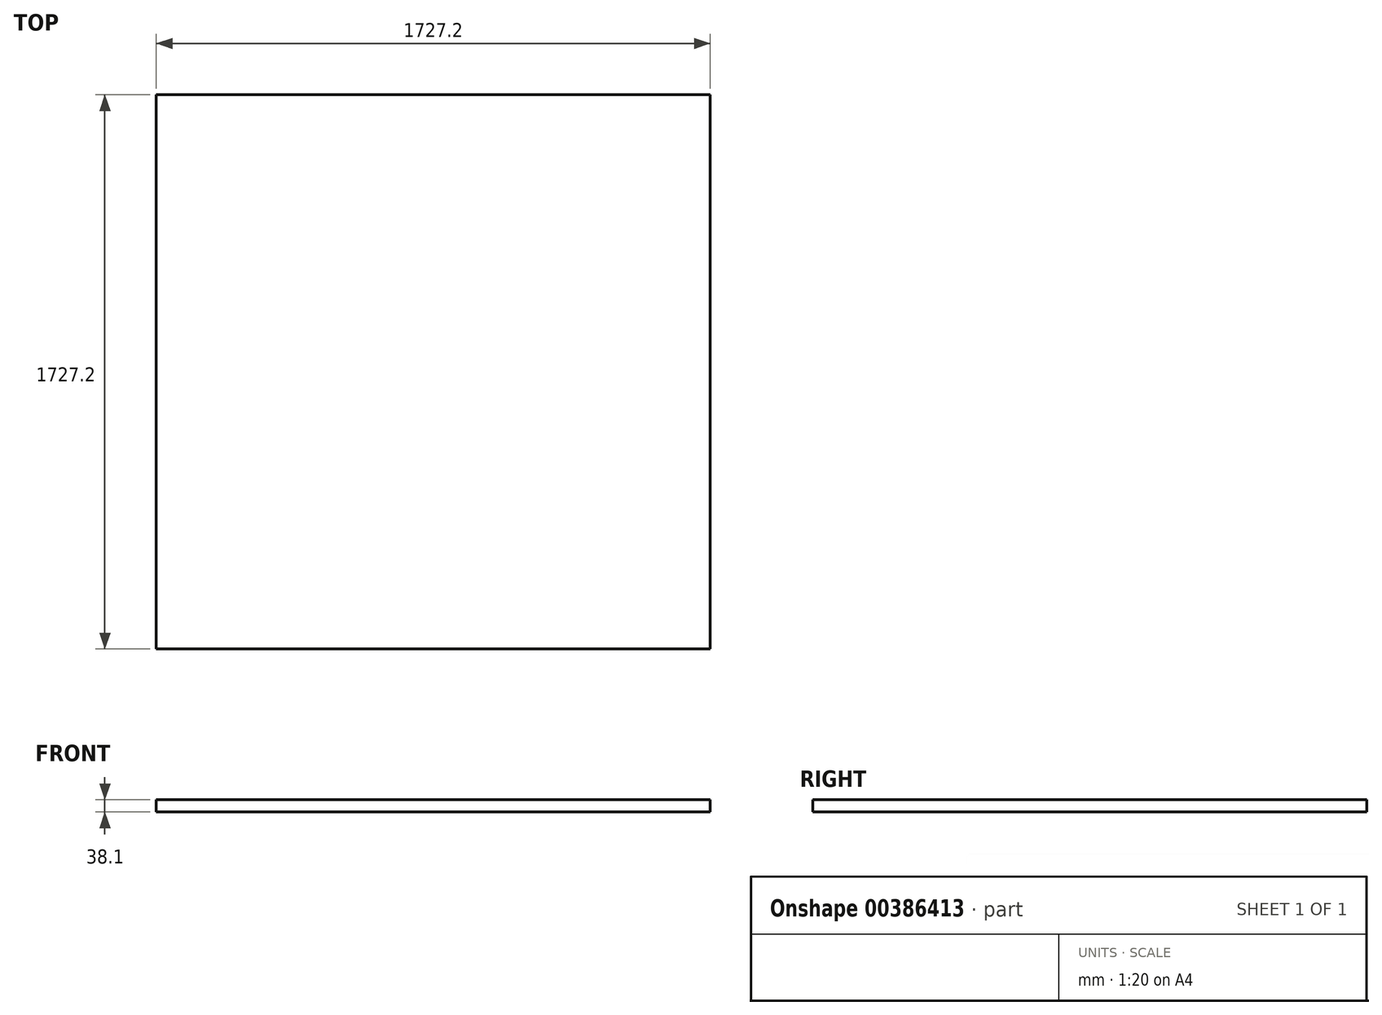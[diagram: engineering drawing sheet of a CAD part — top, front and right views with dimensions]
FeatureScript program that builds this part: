
annotation { "Feature Type Name" : "Feature", "Feature Type Description" : "" }
export const myFeature = defineFeature(function(context is Context, id is Id, definition is map)
    precondition{}
    {
        {
            var Q0;
            Q0=qCreatedBy(makeId("Top.planeOp"),FACE);
            var sketch = newSketch(context, id + "F0", { "sketchPlane" : qUnion([Q0])});
            skLineSegment(sketch, "E0.bottom", {"start": v(-863.6, 863.6) * mm, "end": v(863.6, 863.6) * mm});
            skLineSegment(sketch, "E0.top", {"start": v(-863.6, -863.6) * mm, "end": v(863.6, -863.6) * mm});
            skLineSegment(sketch, "E0.left", {"start": v(-863.6, 863.6) * mm, "end": v(-863.6, -863.6) * mm});
            skLineSegment(sketch, "E0.right", {"start": v(863.6, 863.6) * mm, "end": v(863.6, -863.6) * mm});
            skPoint(sketch, "E0.middle", {"position": v(0, 0) * mm});
            skSolve(sketch);
        }
        {
            var Q0;
            Q0 = qSketchRegion(id + "F0", true);
            extrude(context, id + "F1", {"entities" : qUnion([Q0]), "depth" : 38.1 * mm});
        }
        {
            var Q0;
            Q0=makeQuery(id+"F1.opExtrude","CAP_FACE",FACE,{"disambiguationData":[OSD([sQuery(id+"F0.wireOp",EDGE,"E0.bottom"),sQuery(id+"F0.wireOp",EDGE,"E0.top"),sQuery(id+"F0.wireOp",EDGE,"E0.left"),sQuery(id+"F0.wireOp",EDGE,"E0.right")])],"isStart":false});
            var sketch = newSketch(context, id + "F2", { "sketchPlane" : qUnion([Q0])});
            skLineSegment(sketch, "E1.bottom", {"start": v(-571.5, 571.5) * mm, "end": v(571.5, 571.5) * mm});
            skLineSegment(sketch, "E1.top", {"start": v(-571.5, -571.5) * mm, "end": v(571.5, -571.5) * mm});
            skLineSegment(sketch, "E1.left", {"start": v(-571.5, 571.5) * mm, "end": v(-571.5, -571.5) * mm});
            skLineSegment(sketch, "E1.right", {"start": v(571.5, 571.5) * mm, "end": v(571.5, -571.5) * mm});
            skPoint(sketch, "E1.middle", {"position": v(0, 0) * mm});
            skSolve(sketch);
        }
    });
